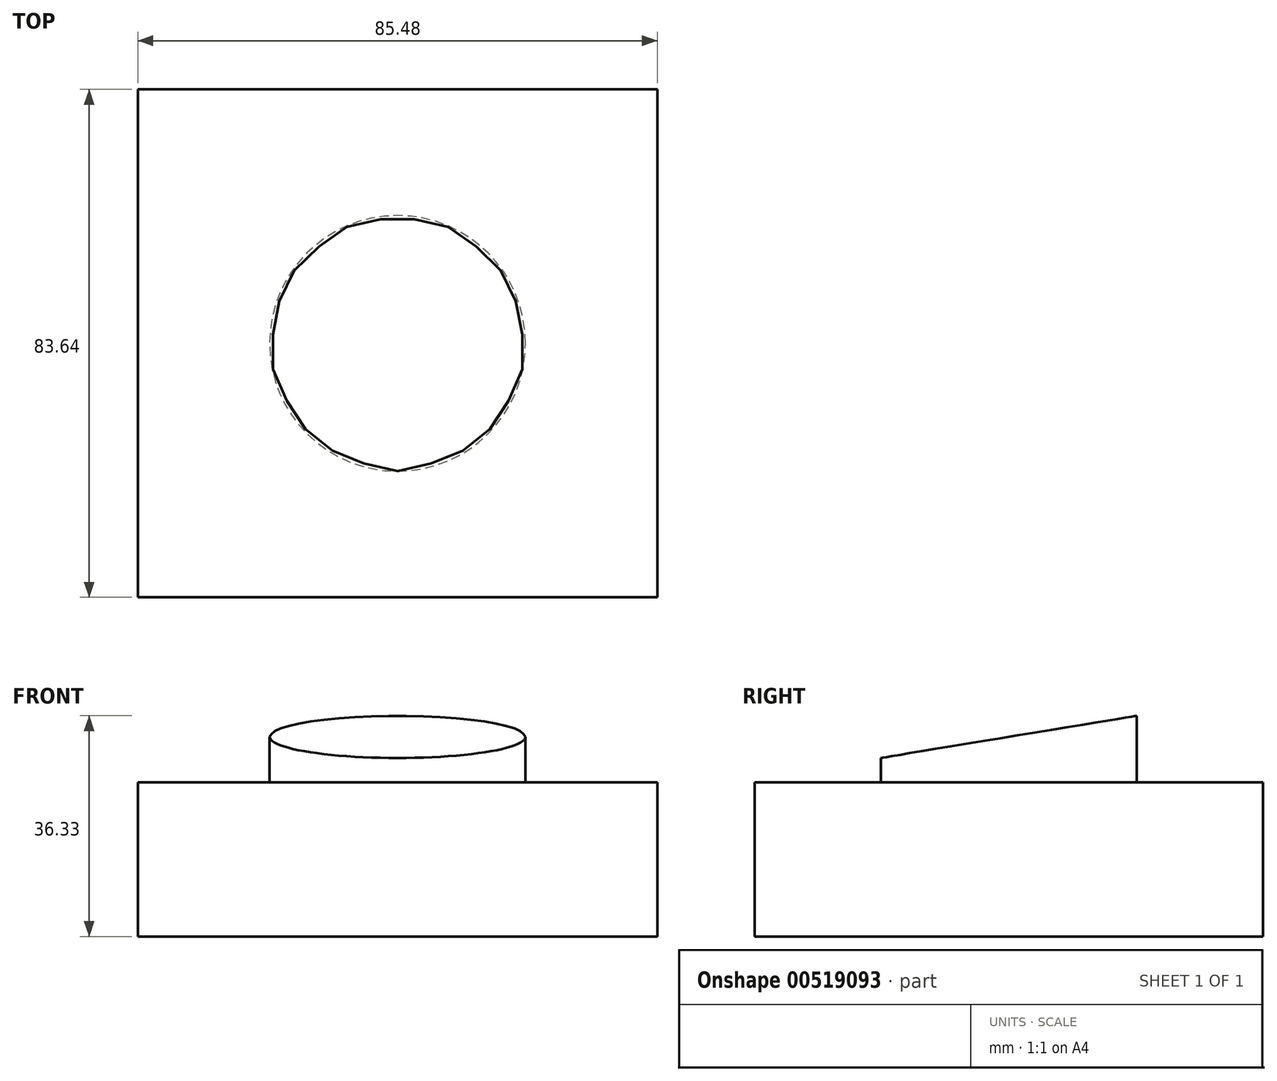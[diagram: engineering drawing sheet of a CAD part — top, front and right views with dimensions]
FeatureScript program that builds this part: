
annotation { "Feature Type Name" : "Feature", "Feature Type Description" : "" }
export const myFeature = defineFeature(function(context is Context, id is Id, definition is map)
    precondition{}
    {
        {
            var Q0;
            Q0=qCreatedBy(makeId("Top.planeOp"),FACE);
            var sketch = newSketch(context, id + "F0", { "sketchPlane" : qUnion([Q0])});
            skLineSegment(sketch, "E0.bottom", {"start": v(42.74, 41.82) * mm, "end": v(-42.74, 41.82) * mm});
            skLineSegment(sketch, "E0.top", {"start": v(42.74, -41.82) * mm, "end": v(-42.74, -41.82) * mm});
            skLineSegment(sketch, "E0.left", {"start": v(42.74, 41.82) * mm, "end": v(42.74, -41.82) * mm});
            skLineSegment(sketch, "E0.right", {"start": v(-42.74, 41.82) * mm, "end": v(-42.74, -41.82) * mm});
            skPoint(sketch, "E0.middle", {"position": v(0, 0) * mm});
            skSolve(sketch);
        }
        {
            var Q0;
            Q0=makeQuery(id+"F0.imprint","IMPRINT",FACE,{"disambiguationData":[TD([[makeQuery(id+"F0.imprint","IMPRINT",EDGE,{"derivedFrom":sQuery(id+"F0.wireOp",EDGE,"E0.bottom")}),1.0]])]});
            var sketch = newSketch(context, id + "F1", { "sketchPlane" : qUnion([Q0])});
            skCircle(sketch, "E1", {"center": v(0, 0) * mm, "radius": 21.05 * mm});
            skSolve(sketch);
        }
        {
            var Q0;
            Q0=makeQuery(id+"F0.imprint","IMPRINT",FACE,{"disambiguationData":[TD([[makeQuery(id+"F0.imprint","IMPRINT",EDGE,{"derivedFrom":sQuery(id+"F0.wireOp",EDGE,"E0.bottom")}),1.0]])]});
            extrude(context, id + "F2", {"entities" : qUnion([Q0]), "depth" : 25.4 * mm});
        }
        {
            var Q0;
            Q0 = qSketchRegion(id + "F1", true);
            extrude(context, id + "F3", {"entities" : qUnion([Q0]), "operationType" : NewBodyOperationType.ADD, "depth" : 44.96 * mm});
        }
        {
            var Q0;
            Q0=qCreatedBy(makeId("Right.planeOp"),FACE);
            var sketch = newSketch(context, id + "F4", { "sketchPlane" : qUnion([Q0])});
            skLineSegment(sketch, "E2", {"start": v(25.42, 48.48) * mm, "end": v(25.42, 37.05) * mm});
            skLineSegment(sketch, "E3", {"start": v(25.42, 37.05) * mm, "end": v(-27.2, 28.38) * mm});
            skLineSegment(sketch, "E4", {"start": v(-27.2, 28.38) * mm, "end": v(-27.2, 49.07) * mm});
            skLineSegment(sketch, "E5", {"start": v(-27.2, 49.07) * mm, "end": v(25.42, 48.48) * mm});
            skSolve(sketch);
        }
        {
            var Q0;
            Q0 = qSketchRegion(id + "F4", true);
            extrude(context, id + "F5", {"entities" : qUnion([Q0]), "operationType" : NewBodyOperationType.REMOVE, "endBound" : BoundingType.SYMMETRIC, "oppositeDirection" : true, "depth" : 65.53 * mm});
        }
    });
